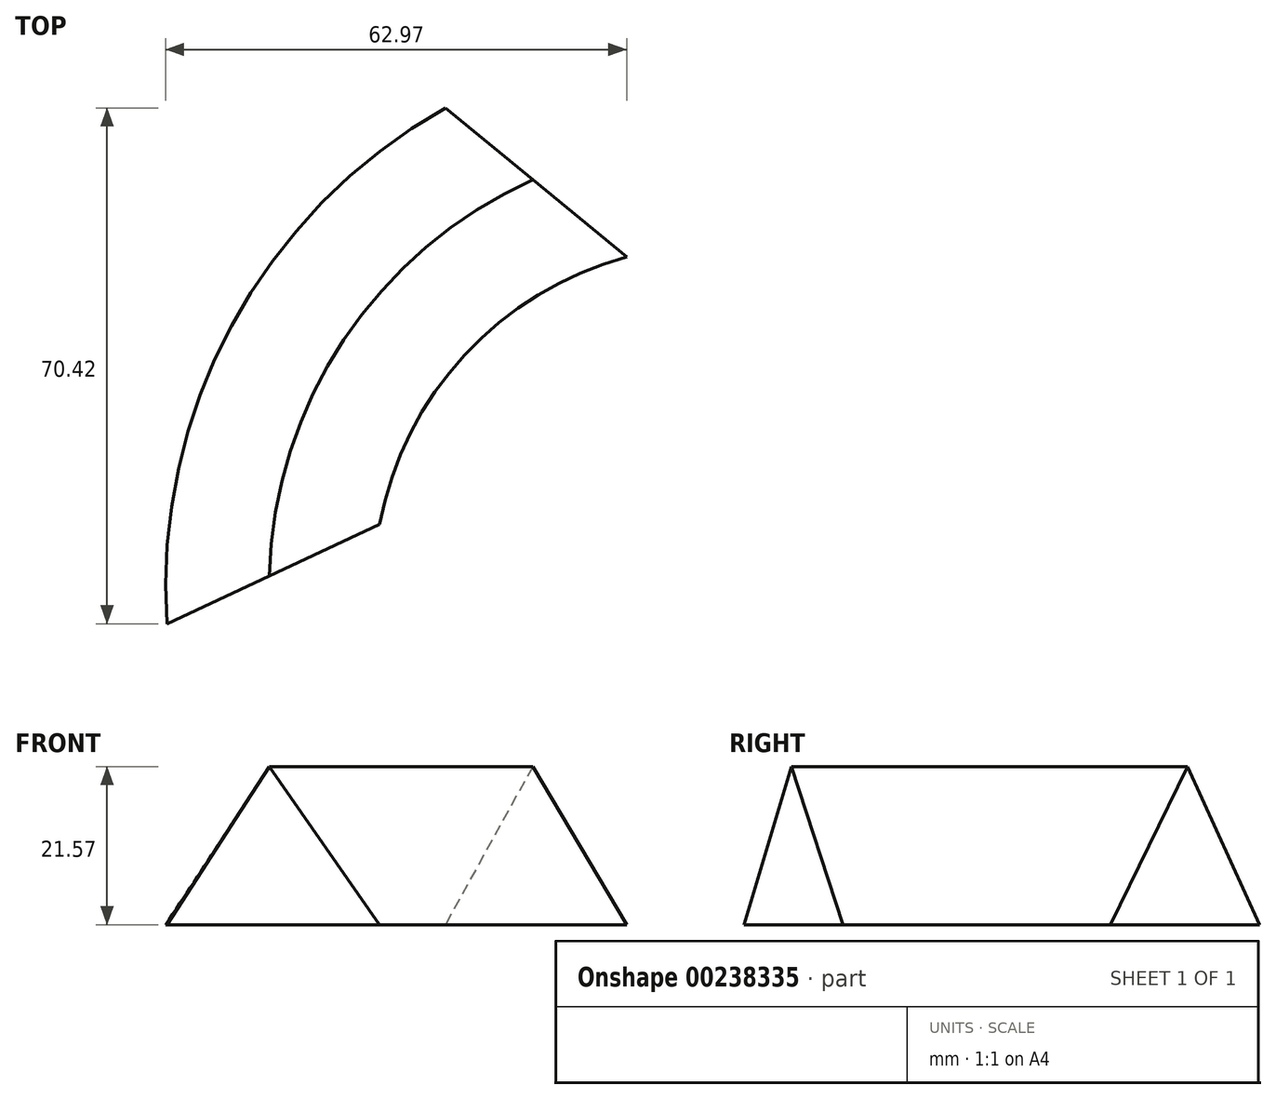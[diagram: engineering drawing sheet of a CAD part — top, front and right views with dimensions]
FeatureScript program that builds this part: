
annotation { "Feature Type Name" : "Feature", "Feature Type Description" : "" }
export const myFeature = defineFeature(function(context is Context, id is Id, definition is map)
    precondition{}
    {
        {
            var Q0;
            Q0=qCreatedBy(makeId("Top.planeOp"),FACE);
            var sketch = newSketch(context, id + "F0", { "sketchPlane" : qUnion([Q0])});
            skArc(sketch, "E0", {"start": v(-15.45, -29.88) * mm, "mid": v(-27.03, 7.66) * mm, "end": v(-53.92, 36.29) * mm});
            skArc(sketch, "E1", {"start": v(21.86, 34.83) * mm, "mid": v(-6.14, 7.87) * mm, "end": v(-15.45, -29.88) * mm});
            skSolve(sketch);
        }
        {
            var Q0;
            Q0=qCreatedBy(makeId("Front.planeOp"),FACE);
            var sketch = newSketch(context, id + "F1", { "sketchPlane" : qUnion([Q0])});
            skLineSegment(sketch, "E2", {"start": v(0, 10.06) * mm, "end": v(-15.45, -11.51) * mm});
            skLineSegment(sketch, "E3", {"start": v(-15.45, -11.51) * mm, "end": v(16.61, -11.51) * mm});
            skLineSegment(sketch, "E4", {"start": v(16.61, -11.51) * mm, "end": v(0, 10.06) * mm});
            skSolve(sketch);
        }
        {
            var Q0;
            Q0=makeQuery(id+"F1.imprint","IMPRINT",FACE,{"disambiguationData":[TD([[makeQuery(id+"F1.imprint","IMPRINT",EDGE,{"derivedFrom":sQuery(id+"F1.wireOp",EDGE,"E2")}),1.0]])]});
            var Q1;
            Q1=sQuery(id+"F0.wireOp",EDGE,"E1");
            sweep(context, id + "F2", {"profiles" : qUnion([Q0]), "path" : qUnion([Q1])});
        }
    });
